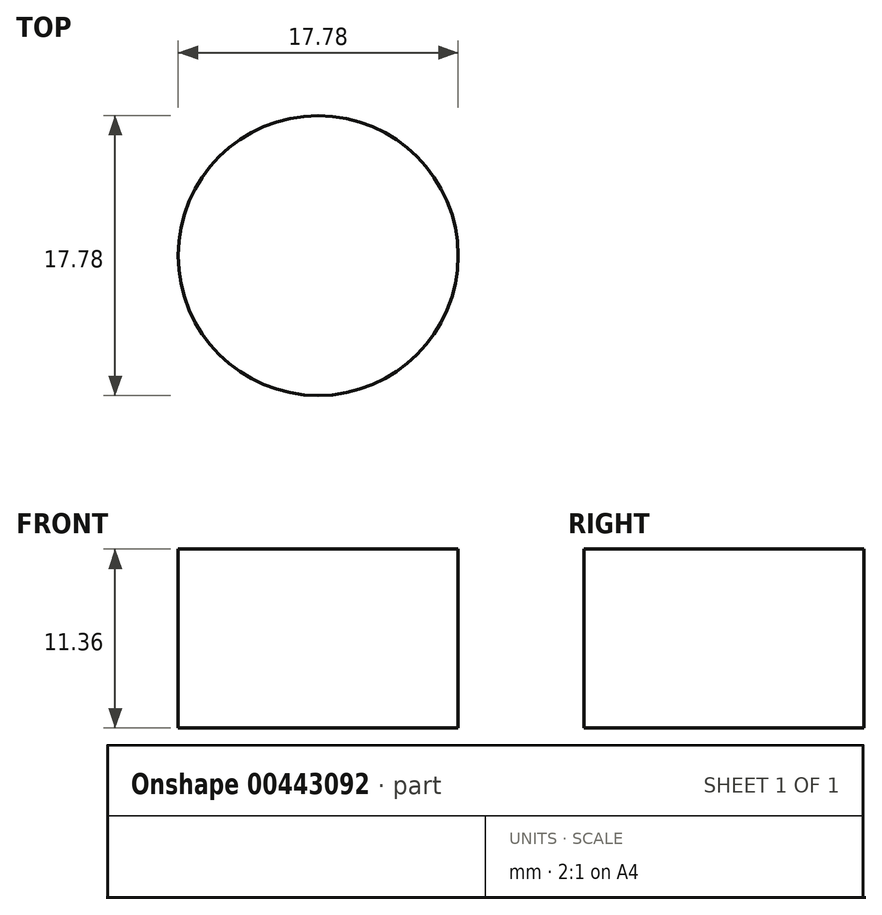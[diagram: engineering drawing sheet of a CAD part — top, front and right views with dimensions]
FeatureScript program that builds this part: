
annotation { "Feature Type Name" : "Feature", "Feature Type Description" : "" }
export const myFeature = defineFeature(function(context is Context, id is Id, definition is map)
    precondition{}
    {
        {
            var Q0;
            Q0=qCreatedBy(makeId("Front.planeOp"),FACE);
            var sketch = newSketch(context, id + "F0", { "sketchPlane" : qUnion([Q0])});
            skLineSegment(sketch, "E0", {"start": v(0, 14.59) * mm, "end": v(-8.9, 14.59) * mm});
            skLineSegment(sketch, "E1", {"start": v(-8.9, 14.59) * mm, "end": v(-8.9, 25.95) * mm});
            skLineSegment(sketch, "E2", {"start": v(-8.9, 25.95) * mm, "end": v(0, 25.95) * mm});
            skLineSegment(sketch, "E3", {"start": v(0, 25.95) * mm, "end": v(0, 14.59) * mm});
            skSolve(sketch);
        }
        {
            var Q0;
            Q0=makeQuery(id+"F0.imprint","IMPRINT",FACE,{"disambiguationData":[TD([[makeQuery(id+"F0.imprint","IMPRINT",EDGE,{"derivedFrom":sQuery(id+"F0.wireOp",EDGE,"E0")}),-1.0]])]});
            var Q1;
            Q1=sQuery(id+"F0.wireOp",EDGE,"E3");
            revolve(context, id + "F1", {"entities" : qUnion([Q0]), "axis" : qUnion([Q1]), "revolveType" : RevolveType.FULL});
        }
    });
